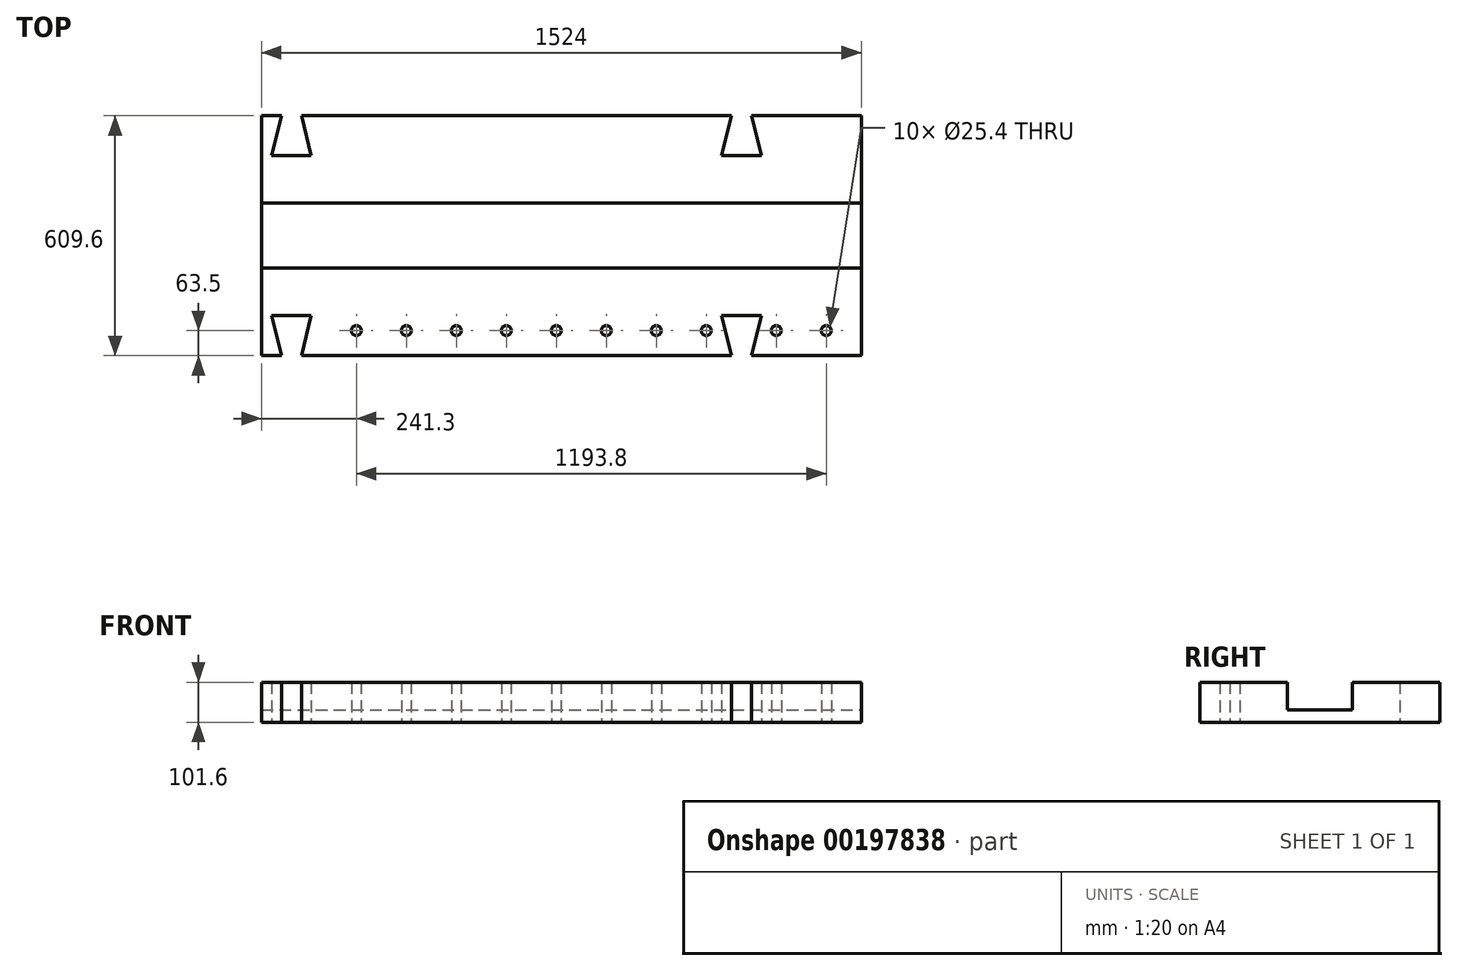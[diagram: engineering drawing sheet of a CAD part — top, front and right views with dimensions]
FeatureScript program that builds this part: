
annotation { "Feature Type Name" : "Feature", "Feature Type Description" : "" }
export const myFeature = defineFeature(function(context is Context, id is Id, definition is map)
    precondition{}
    {
        {
            var Q0;
            Q0=qCreatedBy(makeId("Top.planeOp"),FACE);
            var sketch = newSketch(context, id + "F0", { "sketchPlane" : qUnion([Q0])});
            skLineSegment(sketch, "E0.top", {"start": v(762, 304.8) * mm, "end": v(-762, 304.8) * mm});
            skLineSegment(sketch, "E0.left", {"start": v(762, -304.8) * mm, "end": v(762, 304.8) * mm});
            skLineSegment(sketch, "E0.right", {"start": v(-762, -304.8) * mm, "end": v(-762, 304.8) * mm});
            skPoint(sketch, "E0.middle", {"position": v(0, 0) * mm});
            skLineSegment(sketch, "E1", {"start": v(-762, -304.8) * mm, "end": v(762, -304.8) * mm});
            skLineSegment(sketch, "E2", {"start": v(-736.6, -203.2) * mm, "end": v(-736.6, -304.8) * mm, "construction": true});
            skLineSegment(sketch, "E3", {"start": v(-635, -203.2) * mm, "end": v(-635, -304.8) * mm, "construction": true});
            skLineSegment(sketch, "E4", {"start": v(-635, -304.8) * mm, "end": v(-736.6, -304.8) * mm});
            skLineSegment(sketch, "E5", {"start": v(-736.6, -203.2) * mm, "end": v(-635, -203.2) * mm});
            skLineSegment(sketch, "E6", {"start": v(-685.8, -203.2) * mm, "end": v(-685.8, -304.8) * mm, "construction": true});
            skLineSegment(sketch, "E7", {"start": v(-685.8, -304.8) * mm, "end": v(-711.2, -304.8) * mm});
            skLineSegment(sketch, "E8", {"start": v(-711.2, -304.8) * mm, "end": v(-736.6, -203.2) * mm});
            skLineSegment(sketch, "E9.MirrorCS", {"start": v(-660.4, -304.8) * mm, "end": v(-635, -203.2) * mm});
            skLineSegment(sketch, "E10", {"start": v(-711.2, -304.8) * mm, "end": v(-660.4, -304.8) * mm});
            skLineSegment(sketch, "E11.MirrorCS", {"start": v(431.8, 304.8) * mm, "end": v(406.4, 203.2) * mm});
            skLineSegment(sketch, "E12.MirrorCS", {"start": v(482.6, 304.8) * mm, "end": v(508, 203.2) * mm});
            skLineSegment(sketch, "E13.MirrorCS", {"start": v(431.8, 304.8) * mm, "end": v(482.6, 304.8) * mm});
            skLineSegment(sketch, "E14.MirrorCS", {"start": v(-685.8, 304.8) * mm, "end": v(-711.2, 304.8) * mm});
            skLineSegment(sketch, "E15.MirrorCS", {"start": v(-711.2, 304.8) * mm, "end": v(-660.4, 304.8) * mm});
            skLineSegment(sketch, "E16.MirrorCS", {"start": v(-635, 304.8) * mm, "end": v(-736.6, 304.8) * mm});
            skLineSegment(sketch, "E17.MirrorCS", {"start": v(-736.6, 203.2) * mm, "end": v(-635, 203.2) * mm});
            skLineSegment(sketch, "E18.MirrorCS", {"start": v(-635, 203.2) * mm, "end": v(-635, 304.8) * mm, "construction": true});
            skLineSegment(sketch, "E19.MirrorCS", {"start": v(-736.6, 203.2) * mm, "end": v(-736.6, 304.8) * mm, "construction": true});
            skLineSegment(sketch, "E20.MirrorCS", {"start": v(-685.8, 203.2) * mm, "end": v(-685.8, 304.8) * mm, "construction": true});
            skLineSegment(sketch, "E21.MirrorCS", {"start": v(-660.4, 304.8) * mm, "end": v(-635, 203.2) * mm});
            skLineSegment(sketch, "E22.MirrorCS", {"start": v(-711.2, 304.8) * mm, "end": v(-736.6, 203.2) * mm});
            skLineSegment(sketch, "E23", {"start": v(508, 203.2) * mm, "end": v(508, 304.8) * mm, "construction": true});
            skLineSegment(sketch, "E24", {"start": v(-762, 0) * mm, "end": v(762, 0) * mm, "construction": true});
            skLineSegment(sketch, "E25", {"start": v(406.4, 203.2) * mm, "end": v(508, 203.2) * mm});
            skLineSegment(sketch, "E26.MirrorCS", {"start": v(431.8, -304.8) * mm, "end": v(482.6, -304.8) * mm});
            skLineSegment(sketch, "E27.MirrorCS", {"start": v(406.4, -203.2) * mm, "end": v(508, -203.2) * mm});
            skLineSegment(sketch, "E28.MirrorCS", {"start": v(508, -203.2) * mm, "end": v(508, -304.8) * mm, "construction": true});
            skLineSegment(sketch, "E29.MirrorCS", {"start": v(431.8, -304.8) * mm, "end": v(406.4, -203.2) * mm});
            skLineSegment(sketch, "E30.MirrorCS", {"start": v(482.6, -304.8) * mm, "end": v(508, -203.2) * mm});
            skCircle(sketch, "E31", {"center": v(673.1, -241.3) * mm, "radius": 12.7 * mm});
            skCircle(sketch, "E32", {"center": v(546.1, -241.3) * mm, "radius": 12.7 * mm});
            skLineSegment(sketch, "E33", {"start": v(457.2, -304.8) * mm, "end": v(457.2, -203.2) * mm, "construction": true});
            skCircle(sketch, "E34.MirrorC", {"center": v(368.3, -241.3) * mm, "radius": 12.7 * mm});
            skCircle(sketch, "E35.MirrorC", {"center": v(241.3, -241.3) * mm, "radius": 12.7 * mm});
            skCircle(sketch, "E36.MirrorC", {"center": v(114.3, -241.3) * mm, "radius": 12.7 * mm});
            skCircle(sketch, "E37.MirrorC", {"center": v(-12.7, -241.3) * mm, "radius": 12.7 * mm});
            skCircle(sketch, "E38.MirrorC", {"center": v(-139.7, -241.3) * mm, "radius": 12.7 * mm});
            skCircle(sketch, "E39.MirrorC", {"center": v(-266.7, -241.3) * mm, "radius": 12.7 * mm});
            skCircle(sketch, "E40.MirrorC", {"center": v(-393.7, -241.3) * mm, "radius": 12.7 * mm});
            skCircle(sketch, "E41.MirrorC", {"center": v(-520.7, -241.3) * mm, "radius": 12.7 * mm});
            skSolve(sketch);
        }
        {
            var Q0;
            {var subQ1=sQuery(id+"F0.wireOp",EDGE,"E0.left");Q0=makeQuery(id+"F0.imprint","IMPRINT",FACE,{"disambiguationData":[TD([[makeQuery(id+"F0.imprint","IMPRINT",EDGE,{"derivedFrom":subQ1}),1.0]])]});}
            extrude(context, id + "F1", {"entities" : qUnion([Q0]), "depth" : 101.6 * mm});
        }
        {
            var Q0;
            Q0=makeQuery(id+"F1.opExtrude","CAP_FACE",FACE,{"disambiguationData":[OSD([sQuery(id+"F0.wireOp",EDGE,"E0.top"),sQuery(id+"F0.wireOp",EDGE,"E0.left"),sQuery(id+"F0.wireOp",EDGE,"E0.right"),sQuery(id+"F0.wireOp",EDGE,"EB17UE77-uCtX-zcrS-cqg9-jBA6dNwPmuEu.bottom"),sQuery(id+"F0.wireOp",EDGE,"7SOLYQ0V-MvuG-L3bs-6RDW-NhrBLqCjgoyN"),sQuery(id+"F0.wireOp",EDGE,"33aae0fa-0b08-41e5-a6aa-f49a69d1113a0.MirrorCS"),sQuery(id+"F0.wireOp",EDGE,"51cf615d-c984-4083-a989-8c50b18e5aca1.MirrorCS"),sQuery(id+"F0.wireOp",EDGE,"51cf615d-c984-4083-a989-8c50b18e5aca2.MirrorCS"),sQuery(id+"F0.wireOp",EDGE,"51cf615d-c984-4083-a989-8c50b18e5aca3.MirrorCS"),sQuery(id+"F0.wireOp",EDGE,"5729add0-c551-42ca-b487-860d735ee2f10.MirrorCS"),sQuery(id+"F0.wireOp",EDGE,"5729add0-c551-42ca-b487-860d735ee2f11.MirrorCS"),sQuery(id+"F0.wireOp",EDGE,"5729add0-c551-42ca-b487-860d735ee2f13.MirrorCS"),sQuery(id+"F0.wireOp",EDGE,"d03023e6-bc2c-487b-8238-124c70136cc80.MirrorCS"),sQuery(id+"F0.wireOp",EDGE,"d03023e6-bc2c-487b-8238-124c70136cc81.MirrorCS"),sQuery(id+"F0.wireOp",EDGE,"d03023e6-bc2c-487b-8238-124c70136cc82.MirrorCS"),sQuery(id+"F0.wireOp",EDGE,"E1")])],"isStart":false});
            var sketch = newSketch(context, id + "F2", { "sketchPlane" : qUnion([Q0])});
            skLineSegment(sketch, "E42.0.left", {"start": v(-762, 82.55) * mm, "end": v(762, 82.55) * mm});
            skLineSegment(sketch, "E42.0.right", {"start": v(-762, -82.55) * mm, "end": v(762, -82.55) * mm});
            skLineSegment(sketch, "E43", {"start": v(-762, 82.55) * mm, "end": v(-762, -82.55) * mm});
            skLineSegment(sketch, "E44", {"start": v(762, 82.55) * mm, "end": v(762, -82.55) * mm});
            skLineSegment(sketch, "E45", {"start": v(-762, 0) * mm, "end": v(762, 0) * mm, "construction": true});
            skSolve(sketch);
        }
        {
            var Q0;
            Q0=makeQuery(id+"F2.imprint","IMPRINT",FACE,{"disambiguationData":[TD([[makeQuery(id+"F2.imprint","IMPRINT",EDGE,{"derivedFrom":sQuery(id+"F2.wireOp",EDGE,"E42.0.left")}),-1.0]])]});
            extrude(context, id + "F3", {"entities" : qUnion([Q0]), "operationType" : NewBodyOperationType.REMOVE, "oppositeDirection" : true, "depth" : 69.85 * mm});
        }
    });
